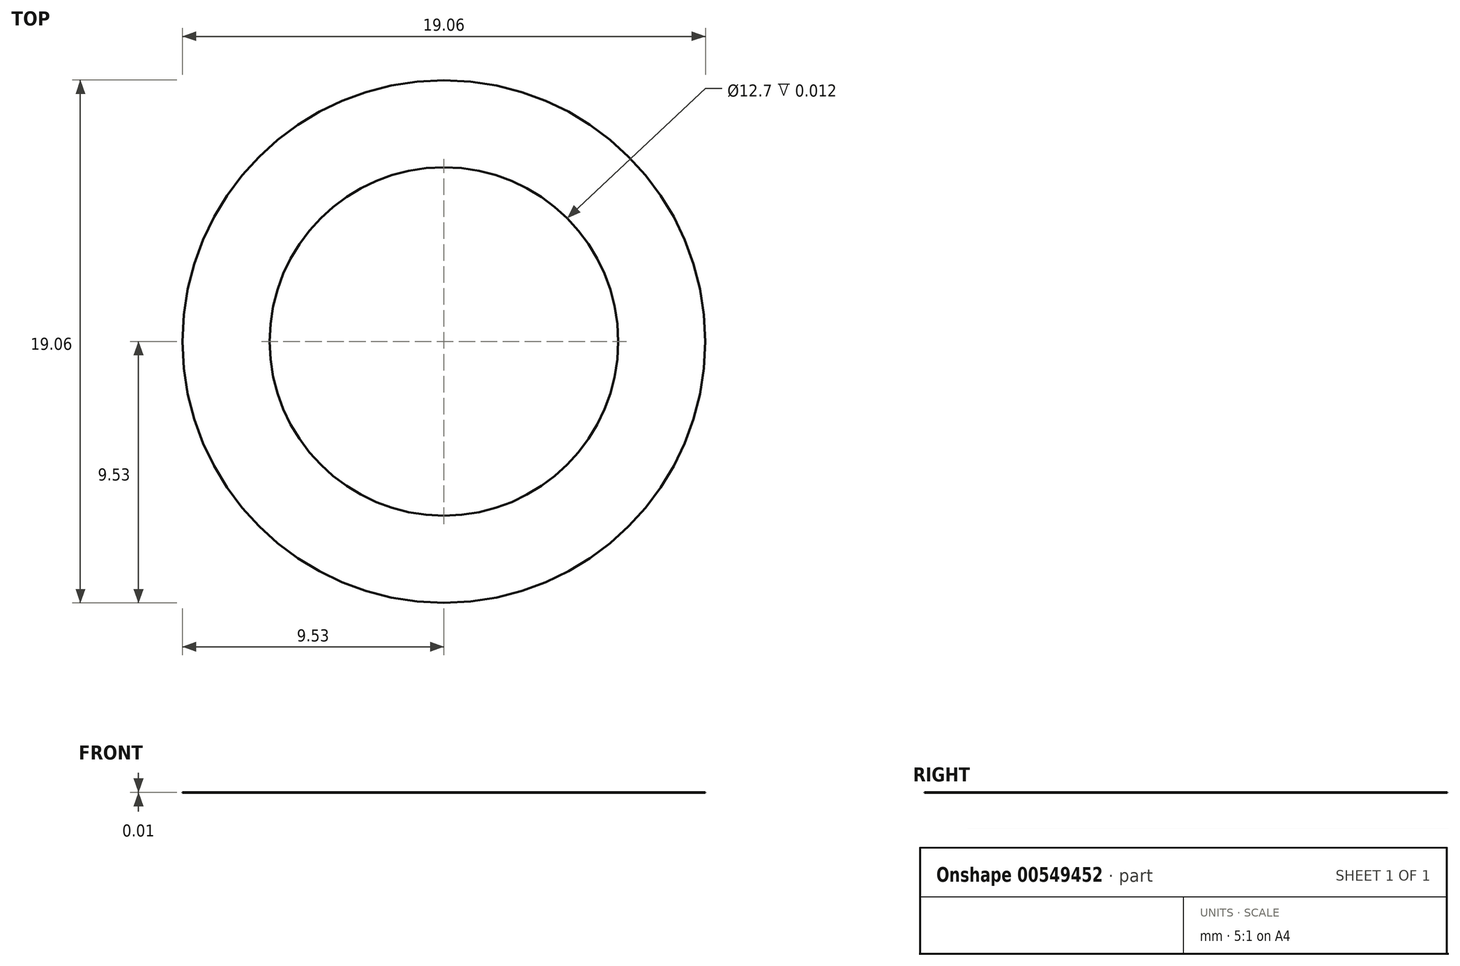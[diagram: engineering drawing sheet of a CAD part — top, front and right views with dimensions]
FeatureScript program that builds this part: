
annotation { "Feature Type Name" : "Feature", "Feature Type Description" : "" }
export const myFeature = defineFeature(function(context is Context, id is Id, definition is map)
    precondition{}
    {
        {
            var Q0;
            Q0=qCreatedBy(makeId("Top.planeOp"),FACE);
            var sketch = newSketch(context, id + "F0", { "sketchPlane" : qUnion([Q0])});
            skCircle(sketch, "E0", {"center": v(0, 0) * mm, "radius": 9.53 * mm});
            skCircle(sketch, "E1", {"center": v(0, 0) * mm, "radius": 6.35 * mm});
            skCircle(sketch, "E2", {"center": v(0, 0) * mm, "radius": 3.97 * mm});
            skSolve(sketch);
        }
        {
            var Q0;
            Q0=makeQuery(id+"F0.imprint","IMPRINT",FACE,{"disambiguationData":[TD([[makeQuery(id+"F0.imprint","IMPRINT",EDGE,{"derivedFrom":sQuery(id+"F0.wireOp",EDGE,"E0")}),1.0]])]});
            var Q1;
            Q1=makeQuery(id+"F0.imprint","IMPRINT",FACE,{"disambiguationData":[TD([[makeQuery(id+"F0.imprint","IMPRINT",EDGE,{"derivedFrom":sQuery(id+"F0.wireOp",EDGE,"E1")}),1.0]])]});
            extrude(context, id + "F1", {"entities" : qUnion([Q0, Q1]), "oppositeDirection" : true, "depth" : 5 / 406.4 * mm, "offsetDistance" : 25.4 * mm});
        }
        {
            var Q0;
            Q0=makeQuery(id+"F0.imprint","IMPRINT",FACE,{"disambiguationData":[TD([[makeQuery(id+"F0.imprint","IMPRINT",EDGE,{"derivedFrom":sQuery(id+"F0.wireOp",EDGE,"E1")}),1.0]])]});
            extrude(context, id + "F2", {"entities" : qUnion([Q0]), "operationType" : NewBodyOperationType.REMOVE, "oppositeDirection" : true, "depth" : 1.27 * mm, "offsetDistance" : 25.4 * mm});
        }
    });
